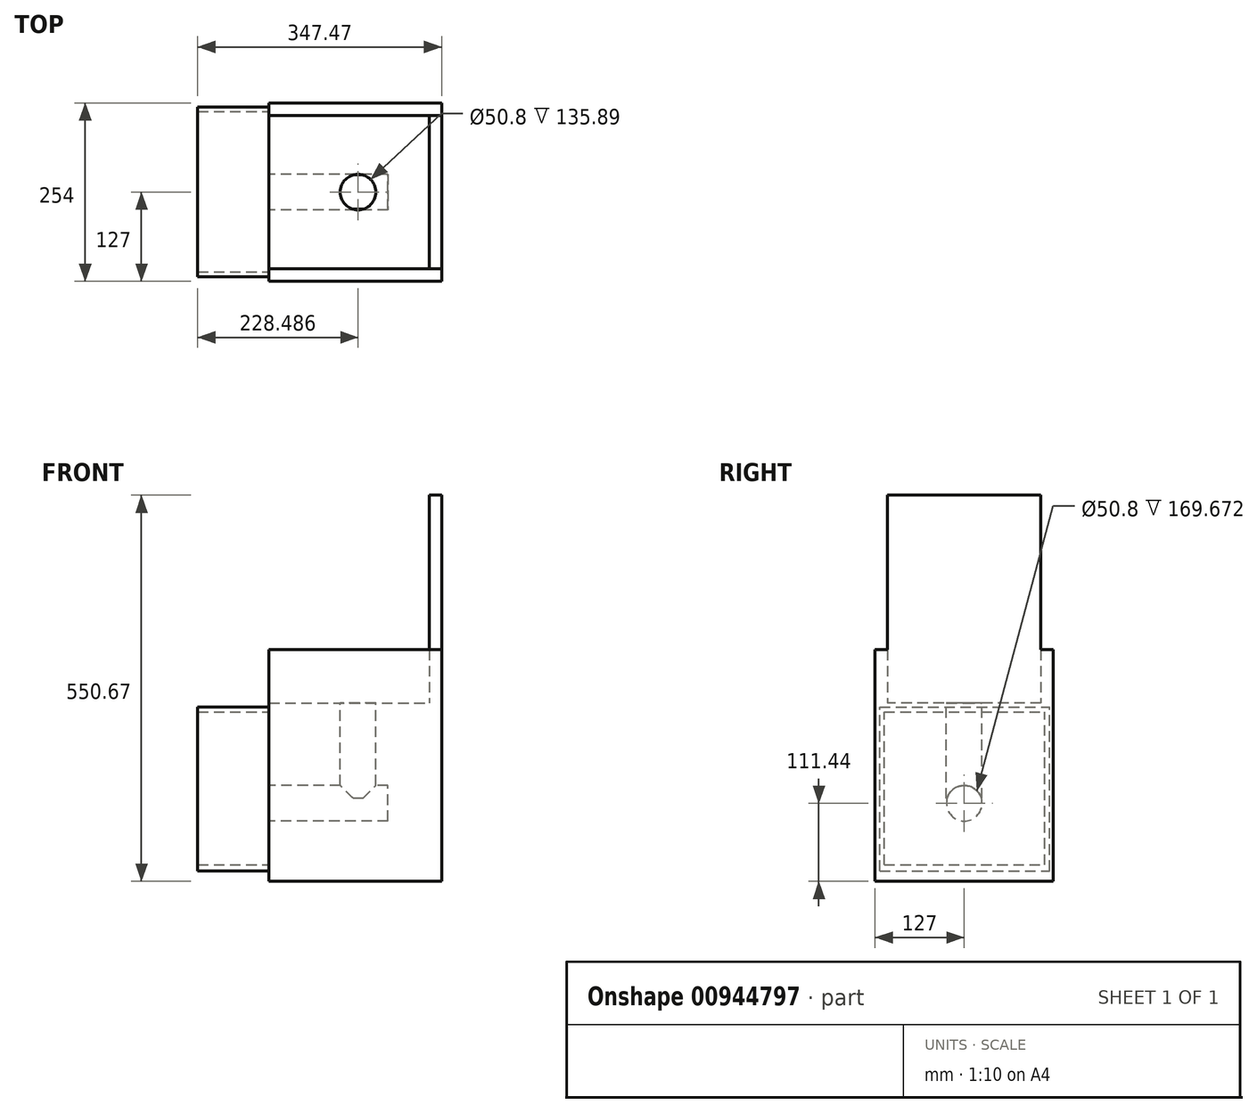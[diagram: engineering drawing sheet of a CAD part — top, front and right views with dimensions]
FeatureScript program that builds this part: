
annotation { "Feature Type Name" : "Feature", "Feature Type Description" : "" }
export const myFeature = defineFeature(function(context is Context, id is Id, definition is map)
    precondition{}
    {
        {
            var Q0;
            Q0=qCreatedBy(makeId("Right.planeOp"),FACE);
            var sketch = newSketch(context, id + "F0", { "sketchPlane" : qUnion([Q0])});
            skLineSegment(sketch, "E0.bottom", {"start": v(-127, 142.56) * mm, "end": v(127, 142.56) * mm});
            skLineSegment(sketch, "E0.top", {"start": v(-127, -111.44) * mm, "end": v(127, -111.44) * mm});
            skLineSegment(sketch, "E0.left", {"start": v(-127, 142.56) * mm, "end": v(-127, -111.44) * mm});
            skLineSegment(sketch, "E0.right", {"start": v(127, 142.56) * mm, "end": v(127, -111.44) * mm});
            skCircle(sketch, "E1", {"center": v(0, 0) * mm, "radius": 25.4 * mm});
            skSolve(sketch);
        }
        {
            var Q0;
            Q0 = qSketchRegion(id + "F0", true);
            var Q1;
            Q1=makeQuery(id+"F0.imprint","IMPRINT",FACE,{"disambiguationData":[TD([[makeQuery(id+"F0.imprint","IMPRINT",EDGE,{"derivedFrom":sQuery(id+"F0.wireOp",EDGE,"E1")}),1.0]])]});
            extrude(context, id + "F1", {"entities" : qUnion([Q0, Q1]), "depth" : 220.47 * mm, "offsetDistance" : 25.4 * mm});
        }
        {
            var Q0;
            Q0=makeQuery(id+"F0.imprint","IMPRINT",FACE,{"disambiguationData":[TD([[makeQuery(id+"F0.imprint","IMPRINT",EDGE,{"derivedFrom":sQuery(id+"F0.wireOp",EDGE,"E1")}),1.0]])]});
            extrude(context, id + "F2", {"entities" : qUnion([Q0]), "operationType" : NewBodyOperationType.REMOVE, "depth" : 144.27 * mm, "offsetDistance" : 25.4 * mm});
        }
        {
            var Q0;
            Q0=makeQuery(id+"F1.opExtrude","SWEPT_FACE",FACE,{"disambiguationData":[OSD([sQuery(id+"F0.wireOp",EDGE,"E0.bottom")])]});
            var sketch = newSketch(context, id + "F3", { "sketchPlane" : qUnion([Q0])});
            skCircle(sketch, "E2", {"center": v(101.49, 0) * mm, "radius": 25.4 * mm});
            skSolve(sketch);
        }
        {
            var Q0;
            Q0 = qSketchRegion(id + "F3", true);
            extrude(context, id + "F4", {"entities" : qUnion([Q0]), "operationType" : NewBodyOperationType.REMOVE, "oppositeDirection" : true, "depth" : 135.89 * mm, "offsetDistance" : 25.4 * mm});
        }
        {
            var Q0;
            Q0=makeQuery(id+"F0.imprint","IMPRINT",FACE,{"disambiguationData":[TD([[makeQuery(id+"F0.imprint","IMPRINT",EDGE,{"derivedFrom":sQuery(id+"F0.wireOp",EDGE,"E0.bottom")}),-1.0]])]});
            var sketch = newSketch(context, id + "F5", { "sketchPlane" : qUnion([Q0])});
            skLineSegment(sketch, "E3.bottom", {"start": v(121.42, 136.97) * mm, "end": v(-120.48, 136.97) * mm});
            skLineSegment(sketch, "E3.top", {"start": v(121.42, -96.5) * mm, "end": v(-120.48, -96.5) * mm});
            skLineSegment(sketch, "E3.left", {"start": v(121.42, 136.97) * mm, "end": v(121.42, -96.5) * mm});
            skLineSegment(sketch, "E3.right", {"start": v(-120.48, 136.97) * mm, "end": v(-120.48, -96.5) * mm});
            skLineSegment(sketch, "E4.bottom", {"start": v(114.9, 129.8) * mm, "end": v(-114.02, 129.8) * mm});
            skLineSegment(sketch, "E4.top", {"start": v(114.9, -87.84) * mm, "end": v(-114.02, -87.84) * mm});
            skLineSegment(sketch, "E4.left", {"start": v(114.9, 129.8) * mm, "end": v(114.9, -87.84) * mm});
            skLineSegment(sketch, "E4.right", {"start": v(-114.02, 129.8) * mm, "end": v(-114.02, -87.84) * mm});
            skLineSegment(sketch, "E5.bottom", {"start": v(109.72, 125.75) * mm, "end": v(-109.72, 125.75) * mm});
            skLineSegment(sketch, "E5.top", {"start": v(109.72, -82) * mm, "end": v(-109.72, -82) * mm});
            skLineSegment(sketch, "E5.left", {"start": v(109.72, 125.75) * mm, "end": v(109.72, -82) * mm});
            skLineSegment(sketch, "E5.right", {"start": v(-109.72, 125.75) * mm, "end": v(-109.72, -82) * mm});
            skSolve(sketch);
        }
        {
            var Q0;
            Q0 = qSketchRegion(id + "F5", true);
            extrude(context, id + "F6", {"entities" : qUnion([Q0]), "operationType" : NewBodyOperationType.ADD, "oppositeDirection" : true, "depth" : 101.6 * mm, "offsetDistance" : 25.4 * mm});
        }
        {
            var Q0;
            Q0=makeQuery(id+"F6.opExtrude","CAP_FACE",FACE,{"disambiguationData":[OSD([sQuery(id+"F5.wireOp",EDGE,"E3.bottom"),sQuery(id+"F5.wireOp",EDGE,"E3.top"),sQuery(id+"F5.wireOp",EDGE,"E3.left"),sQuery(id+"F5.wireOp",EDGE,"E3.right"),sQuery(id+"F5.wireOp",EDGE,"E4.bottom"),sQuery(id+"F5.wireOp",EDGE,"E4.top"),sQuery(id+"F5.wireOp",EDGE,"E4.left"),sQuery(id+"F5.wireOp",EDGE,"E4.right")])],"isStart":false});
            var Q1;
            Q1=makeQuery(id+"F0.imprint","IMPRINT",FACE,{"disambiguationData":[TD([[makeQuery(id+"F0.imprint","IMPRINT",EDGE,{"derivedFrom":sQuery(id+"F0.wireOp",EDGE,"E0.bottom")}),-1.0]])]});
            extrude(context, id + "F7", {"entities" : qUnion([Q0, Q1]), "operationType" : NewBodyOperationType.ADD, "depth" : 25.4 * mm, "offsetDistance" : 25.4 * mm});
        }
        {
            var Q0;
            {var subQ0=sQuery(id+"F0.wireOp",EDGE,"E0.bottom");Q0=makeQuery(id+"F7.boolean.opBoolean","MERGE",FACE,{"derivedFrom":[makeQuery(id+"F1.opExtrude","SWEPT_FACE",FACE,{"disambiguationData":[OSD([subQ0])]}),makeQuery(id+"F7.opExtrude","SWEPT_FACE",FACE,{"disambiguationData":[OSD([subQ0])]})]});}
            var sketch = newSketch(context, id + "F8", { "sketchPlane" : qUnion([Q0])});
            skLineSegment(sketch, "E6.bottom", {"start": v(-25.4, 127) * mm, "end": v(220.47, 127) * mm});
            skLineSegment(sketch, "E6.top", {"start": v(-25.4, 109.22) * mm, "end": v(220.47, 109.22) * mm});
            skLineSegment(sketch, "E6.left", {"start": v(-25.4, 127) * mm, "end": v(-25.4, 109.22) * mm});
            skLineSegment(sketch, "E6.right", {"start": v(220.47, 127) * mm, "end": v(220.47, 109.22) * mm});
            skLineSegment(sketch, "E7.bottom", {"start": v(-25.4, -127) * mm, "end": v(220.47, -127) * mm});
            skLineSegment(sketch, "E7.top", {"start": v(-25.4, -109.22) * mm, "end": v(220.47, -109.22) * mm});
            skLineSegment(sketch, "E7.left", {"start": v(-25.4, -127) * mm, "end": v(-25.4, -109.22) * mm});
            skLineSegment(sketch, "E7.right", {"start": v(220.47, -127) * mm, "end": v(220.47, -109.22) * mm});
            skLineSegment(sketch, "E8.bottom", {"start": v(202.78, 127) * mm, "end": v(220.47, 127) * mm});
            skLineSegment(sketch, "E8.top", {"start": v(202.78, -127) * mm, "end": v(220.47, -127) * mm});
            skLineSegment(sketch, "E8.left", {"start": v(202.78, 127) * mm, "end": v(202.78, -127) * mm});
            skLineSegment(sketch, "E8.right", {"start": v(220.47, 127) * mm, "end": v(220.47, -127) * mm});
            skSolve(sketch);
        }
        {
            var Q0;
            {var subQ0=sQuery(id+"F8.wireOp",EDGE,"E6.bottom");Q0=makeQuery(id+"F8.imprint","IMPRINT",FACE,{"disambiguationData":[TD([[makeQuery(id+"F8.imprint","IMPRINT",EDGE,{"derivedFrom":subQ0}),1.0]])]});}
            var Q1;
            {var subQ5=sQuery(id+"F8.wireOp",EDGE,"E8.bottom");Q1=makeQuery(id+"F8.imprint","IMPRINT",FACE,{"disambiguationData":[TD([[makeQuery(id+"F8.imprint","IMPRINT",EDGE,{"derivedFrom":subQ5}),1.0]])]});}
            var Q2;
            {var subQ0=sQuery(id+"F8.wireOp",EDGE,"E7.bottom");Q2=makeQuery(id+"F8.imprint","IMPRINT",FACE,{"disambiguationData":[TD([[makeQuery(id+"F8.imprint","IMPRINT",EDGE,{"derivedFrom":subQ0}),-1.0]])]});}
            var Q3;
            {var subQ5=sQuery(id+"F8.wireOp",EDGE,"E8.top");Q3=makeQuery(id+"F8.imprint","IMPRINT",FACE,{"disambiguationData":[TD([[makeQuery(id+"F8.imprint","IMPRINT",EDGE,{"derivedFrom":subQ5}),-1.0]])]});}
            extrude(context, id + "F9", {"entities" : qUnion([Q0, Q1, Q2, Q3]), "operationType" : NewBodyOperationType.ADD, "depth" : 76.2 * mm, "offsetDistance" : 25.4 * mm});
        }
        {
            var Q0;
            {var subQ0=sQuery(id+"F8.wireOp",EDGE,"E8.right");var subQ1=sQuery(id+"F8.wireOp",EDGE,"E6.top");var subQ2=makeQuery(id+"F8.imprint","INTERSECT",VERTEX,{"derivedFrom":[subQ1,subQ0]});Q0=makeQuery(id+"F8.imprint","IMPRINT",FACE,{"disambiguationData":[TD([[makeQuery(id+"F8.imprint","IMPRINT",EDGE,{"disambiguationData":[TD([[subQ2,1.0]])],"derivedFrom":subQ1}),-1.0]])]});}
            extrude(context, id + "F10", {"entities" : qUnion([Q0]), "operationType" : NewBodyOperationType.ADD, "depth" : 296.67 * mm, "offsetDistance" : 25.4 * mm});
        }
    });
